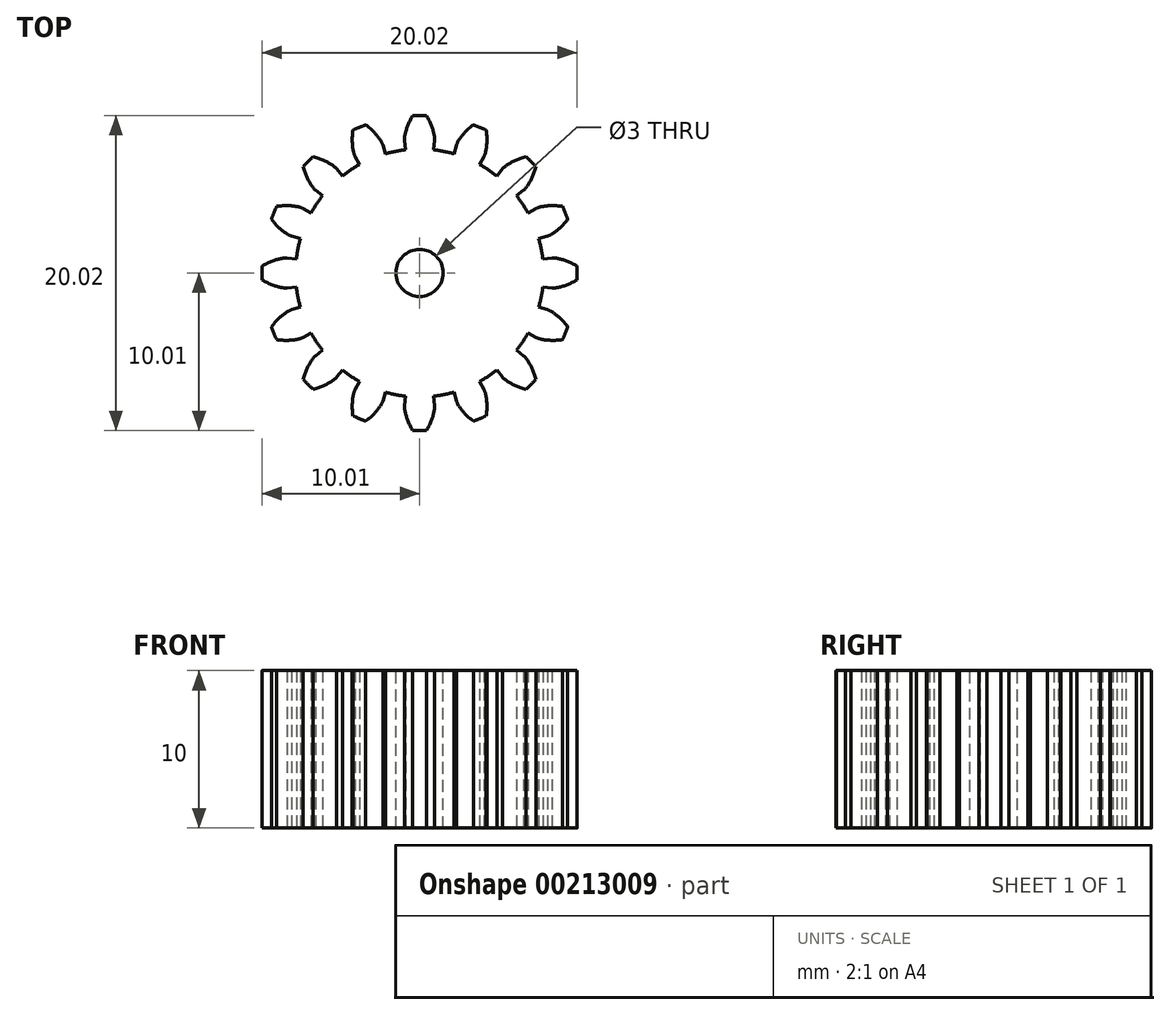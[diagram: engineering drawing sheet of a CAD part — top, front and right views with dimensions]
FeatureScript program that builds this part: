
annotation { "Feature Type Name" : "Feature", "Feature Type Description" : "" }
export const myFeature = defineFeature(function(context is Context, id is Id, definition is map)
    precondition{}
    {
        {
            var Q0;
            Q0=qCreatedBy(makeId("Top.planeOp"),FACE);
            var sketch = newSketch(context, id + "F0", { "sketchPlane" : qUnion([Q0])});
            skCircle(sketch, "E0", {"center": v(0, 0) * mm, "radius": 8.46 * mm, "construction": true});
            skLineSegment(sketch, "E1", {"start": v(8.46, 0) * mm, "end": v(8.46, 0) * mm});
            skLineSegment(sketch, "E2", {"start": v(0, 0) * mm, "end": v(8.44, 0.55) * mm, "construction": true});
            skLineSegment(sketch, "E3", {"start": v(8.44, 0.55) * mm, "end": v(8.47, 0) * mm, "construction": true});
            skLineSegment(sketch, "E4", {"start": v(0, 0) * mm, "end": v(8.39, 1.09) * mm, "construction": true});
            skLineSegment(sketch, "E5", {"start": v(8.39, 1.09) * mm, "end": v(8.53, 0) * mm, "construction": true});
            skLineSegment(sketch, "E6", {"start": v(0, 0) * mm, "end": v(8.3, 1.63) * mm, "construction": true});
            skLineSegment(sketch, "E7", {"start": v(8.3, 1.63) * mm, "end": v(8.61, 0.02) * mm, "construction": true});
            skLineSegment(sketch, "E8", {"start": v(0, 0) * mm, "end": v(8.18, 2.16) * mm, "construction": true});
            skLineSegment(sketch, "E9", {"start": v(8.18, 2.16) * mm, "end": v(8.73, 0.05) * mm, "construction": true});
            skLineSegment(sketch, "E10", {"start": v(0, 0) * mm, "end": v(8.02, 2.68) * mm, "construction": true});
            skLineSegment(sketch, "E11", {"start": v(8.02, 2.68) * mm, "end": v(8.89, 0.1) * mm, "construction": true});
            skLineSegment(sketch, "E12", {"start": v(0, 0) * mm, "end": v(7.83, 3.2) * mm, "construction": true});
            skLineSegment(sketch, "E13", {"start": v(7.83, 3.2) * mm, "end": v(9.07, 0.16) * mm, "construction": true});
            skLineSegment(sketch, "E14", {"start": v(0, 0) * mm, "end": v(7.6, 3.7) * mm, "construction": true});
            skLineSegment(sketch, "E15", {"start": v(7.6, 3.7) * mm, "end": v(9.28, 0.26) * mm, "construction": true});
            skLineSegment(sketch, "E16", {"start": v(0, 0) * mm, "end": v(7.35, 4.18) * mm, "construction": true});
            skLineSegment(sketch, "E17", {"start": v(7.35, 4.18) * mm, "end": v(9.51, 0.38) * mm, "construction": true});
            skLineSegment(sketch, "E18", {"start": v(0, 0) * mm, "end": v(7.07, 4.64) * mm, "construction": true});
            skLineSegment(sketch, "E19", {"start": v(7.07, 4.64) * mm, "end": v(9.77, 0.53) * mm, "construction": true});
            skLineSegment(sketch, "E20", {"start": v(0, 0) * mm, "end": v(6.75, 5.09) * mm, "construction": true});
            skLineSegment(sketch, "E21", {"start": v(6.75, 5.09) * mm, "end": v(10.04, 0.73) * mm, "construction": true});
            skPoint(sketch, "E22", {"position": v(8.46, 0) * mm});
            skCircle(sketch, "E23", {"center": v(0, 0) * mm, "radius": 7.87 * mm});
            skLineSegment(sketch, "E24", {"start": v(7.87, 0) * mm, "end": v(8.46, 0) * mm});
            skFitSpline(sketch, "E25", {"points": [v(8.46, 0) * mm, v(8.47, 0) * mm, v(8.53, 0) * mm, v(8.61, 0.02) * mm, v(8.73, 0.05) * mm, v(8.89, 0.1) * mm, v(9.07, 0.16) * mm, v(9.28, 0.26) * mm, v(9.51, 0.38) * mm, v(9.77, 0.53) * mm, v(10.04, 0.73) * mm], "startDerivative": vector(0.46, 0.01) * mm, "endDerivative": vector(1.88, 1.36) * mm});
            skFitSpline(sketch, "E26", {"points": [v(8.46, 0) * mm, v(8.47, 0) * mm, v(8.53, 0) * mm, v(8.61, 0.02) * mm, v(8.73, 0.05) * mm, v(8.89, 0.1) * mm, v(9.07, 0.16) * mm, v(9.28, 0.26) * mm, v(9.51, 0.38) * mm, v(9.77, 0.53) * mm, v(10.04, 0.73) * mm], "startDerivative": vector(0.46, 0.01) * mm, "endDerivative": vector(1.88, 1.36) * mm, "construction": true});
            skLineSegment(sketch, "E27", {"start": v(0, 0) * mm, "end": v(11.88, 1.35) * mm, "construction": true});
            skLineSegment(sketch, "E28.MirrorCS", {"start": v(7.67, 1.77) * mm, "end": v(8.24, 1.9) * mm});
            skFitSpline(sketch, "E29.MirrorCS", {"points": [v(8.24, 1.9) * mm, v(8.26, 1.9) * mm, v(8.31, 1.9) * mm, v(8.4, 1.91) * mm, v(8.52, 1.91) * mm, v(8.68, 1.9) * mm, v(8.87, 1.88) * mm, v(9.1, 1.83) * mm, v(9.35, 1.76) * mm, v(9.64, 1.67) * mm, v(9.95, 1.54) * mm], "startDerivative": vector(0.45, 0.1) * mm, "endDerivative": vector(2.14, -0.9) * mm});
            skArc(sketch, "E30", {"start": v(9.89, 1.57) * mm, "mid": v(-9.95, -1.13) * mm, "end": v(9.99, 0.7) * mm, "construction": true});
            skArc(sketch, "E31", {"start": v(9.99, 0.7) * mm, "mid": v(9.95, 1.13) * mm, "end": v(9.89, 1.57) * mm});
            skSolve(sketch);
        }
        {
            var Q0;
            {var subQ0=sQuery(id+"F0.wireOp",EDGE,"E23");var subQ1=makeQuery(id+"F0.imprint","INTERSECT",VERTEX,{"derivedFrom":[subQ0,sQuery(id+"F0.wireOp",EDGE,"E24")]});Q0=makeQuery(id+"F0.imprint","IMPRINT",FACE,{"disambiguationData":[TD([[makeQuery(id+"F0.imprint","IMPRINT",EDGE,{"disambiguationData":[TD([[subQ1,-1.0]])],"derivedFrom":subQ0}),1.0]])]});}
            var Q1;
            {var subQ1=sQuery(id+"F0.wireOp",EDGE,"E24");Q1=makeQuery(id+"F0.imprint","IMPRINT",FACE,{"disambiguationData":[TD([[makeQuery(id+"F0.imprint","IMPRINT",EDGE,{"derivedFrom":subQ1}),1.0]])]});}
            extrude(context, id + "F1", {"entities" : qUnion([Q0, Q1]), "depth" : 10 * mm, "symmetric" : true});
        }
        {
            var Q0;
            Q0=qCreatedBy(makeId("Front.planeOp"),FACE);
            var sketch = newSketch(context, id + "F2", { "sketchPlane" : qUnion([Q0])});
            skLineSegment(sketch, "E32", {"start": v(0, 0) * mm, "end": v(0, 27.08) * mm});
            skSolve(sketch);
        }
        {
            var Q0;
            Q0=makeQuery(id+"F1.opExtrude","SWEPT_BODY",BODY,{"disambiguationData":[OSD([sQuery(id+"F0.wireOp",EDGE,"E23"),sQuery(id+"F0.wireOp",EDGE,"E24"),sQuery(id+"F0.wireOp",EDGE,"E25"),sQuery(id+"F0.wireOp",EDGE,"E28.MirrorCS"),sQuery(id+"F0.wireOp",EDGE,"E29.MirrorCS"),sQuery(id+"F0.wireOp",EDGE,"E31")])]});
            var Q1;
            Q1=sQuery(id+"F2.wireOp",EDGE,"E32");
            circularPattern(context, id + "F3", {"operationType" : NewBodyOperationType.ADD, "entities" : qUnion([Q0]), "axis" : qUnion([Q1]), "angle" : 360 * degree, "instanceCount" : 16, "equalSpace" : true});
        }
        {
            var Q0;
            {var subQ0=makeQuery(id+"F1.opExtrude","CAP_FACE",FACE,{"disambiguationData":[OSD([sQuery(id+"F0.wireOp",EDGE,"E23"),sQuery(id+"F0.wireOp",EDGE,"E24"),sQuery(id+"F0.wireOp",EDGE,"E25"),sQuery(id+"F0.wireOp",EDGE,"E28.MirrorCS"),sQuery(id+"F0.wireOp",EDGE,"E29.MirrorCS"),sQuery(id+"F0.wireOp",EDGE,"E31")])],"isStart":false});Q0=makeQuery(id+"F3.boolean.opBoolean","MERGE",FACE,{"derivedFrom":[subQ0,makeQuery(id+"F3.opPattern","COPY",FACE,{"derivedFrom":subQ0,"instanceName":"1"}),makeQuery(id+"F3.opPattern","COPY",FACE,{"derivedFrom":subQ0,"instanceName":"2"}),makeQuery(id+"F3.opPattern","COPY",FACE,{"derivedFrom":subQ0,"instanceName":"3"}),makeQuery(id+"F3.opPattern","COPY",FACE,{"derivedFrom":subQ0,"instanceName":"4"}),makeQuery(id+"F3.opPattern","COPY",FACE,{"derivedFrom":subQ0,"instanceName":"5"}),makeQuery(id+"F3.opPattern","COPY",FACE,{"derivedFrom":subQ0,"instanceName":"6"}),makeQuery(id+"F3.opPattern","COPY",FACE,{"derivedFrom":subQ0,"instanceName":"7"}),makeQuery(id+"F3.opPattern","COPY",FACE,{"derivedFrom":subQ0,"instanceName":"8"}),makeQuery(id+"F3.opPattern","COPY",FACE,{"derivedFrom":subQ0,"instanceName":"9"}),makeQuery(id+"F3.opPattern","COPY",FACE,{"derivedFrom":subQ0,"instanceName":"10"}),makeQuery(id+"F3.opPattern","COPY",FACE,{"derivedFrom":subQ0,"instanceName":"11"}),makeQuery(id+"F3.opPattern","COPY",FACE,{"derivedFrom":subQ0,"instanceName":"12"}),makeQuery(id+"F3.opPattern","COPY",FACE,{"derivedFrom":subQ0,"instanceName":"13"}),makeQuery(id+"F3.opPattern","COPY",FACE,{"derivedFrom":subQ0,"instanceName":"14"}),makeQuery(id+"F3.opPattern","COPY",FACE,{"derivedFrom":subQ0,"instanceName":"15"})]});}
            var sketch = newSketch(context, id + "F4", { "sketchPlane" : qUnion([Q0])});
            skCircle(sketch, "E33", {"center": v(0, 0) * mm, "radius": 1.5 * mm});
            skSolve(sketch);
        }
        {
            var Q0;
            Q0=makeQuery(id+"F4.imprint","IMPRINT",FACE,{"disambiguationData":[TD([[makeQuery(id+"F4.imprint","IMPRINT",EDGE,{"derivedFrom":sQuery(id+"F4.wireOp",EDGE,"E33")}),1.0]])]});
            extrude(context, id + "F5", {"entities" : qUnion([Q0]), "operationType" : NewBodyOperationType.REMOVE, "endBound" : BoundingType.UP_TO_NEXT, "oppositeDirection" : true, "depth" : 25 * mm});
        }
        {
            var Q0;
            Q0=makeQuery(id+"F1.opExtrude","SWEPT_BODY",BODY,{"disambiguationData":[OSD([sQuery(id+"F0.wireOp",EDGE,"E23"),sQuery(id+"F0.wireOp",EDGE,"E24"),sQuery(id+"F0.wireOp",EDGE,"E25"),sQuery(id+"F0.wireOp",EDGE,"E28.MirrorCS"),sQuery(id+"F0.wireOp",EDGE,"E29.MirrorCS"),sQuery(id+"F0.wireOp",EDGE,"E31")])]});
            var Q1;
            Q1=sQuery(id+"F2.wireOp",EDGE,"E32");
            transform(context, id + "F6", {"entities" : qUnion([Q0]), "transformType" : TransformType.ROTATION, "transformAxis" : qUnion([Q1]), "angle" : 6.48 * degree, "oppositeDirection" : true, "makeCopy" : false});
        }
    });
